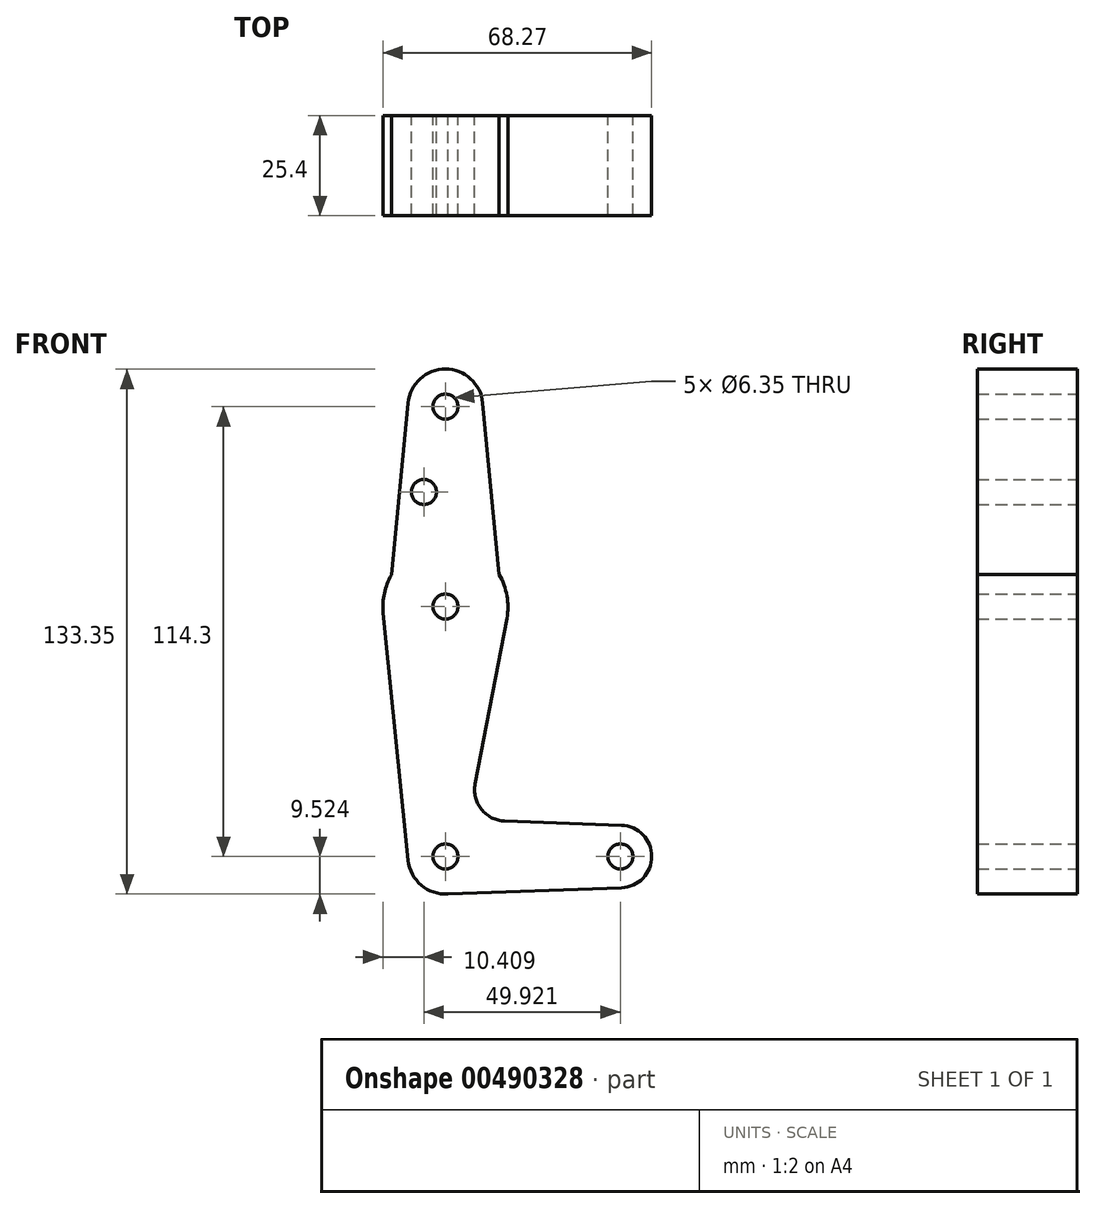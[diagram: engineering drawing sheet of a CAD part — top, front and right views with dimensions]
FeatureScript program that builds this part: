
annotation { "Feature Type Name" : "Feature", "Feature Type Description" : "" }
export const myFeature = defineFeature(function(context is Context, id is Id, definition is map)
    precondition{}
    {
        {
            var Q0;
            Q0=qCreatedBy(makeId("Front.planeOp"),FACE);
            var sketch = newSketch(context, id + "F0", { "sketchPlane" : qUnion([Q0])});
            skLineSegment(sketch, "E0", {"start": v(0, 62.8) * mm, "end": v(0, -51.5) * mm});
            skLineSegment(sketch, "E1", {"start": v(0, -51.5) * mm, "end": v(44.45, -51.5) * mm});
            skCircle(sketch, "E2", {"center": v(0, 62.8) * mm, "radius": 9.53 * mm});
            skCircle(sketch, "E3", {"center": v(0, 12) * mm, "radius": 15.88 * mm});
            skCircle(sketch, "E4", {"center": v(0, -51.5) * mm, "radius": 9.53 * mm});
            skCircle(sketch, "E5", {"center": v(44.45, -51.5) * mm, "radius": 7.94 * mm});
            skLineSegment(sketch, "E6", {"start": v(15.6, 9) * mm, "end": v(7.53, -33.08) * mm});
            skLineSegment(sketch, "E7", {"start": v(-9.48, 63.71) * mm, "end": v(-13.71, 20) * mm});
            skLineSegment(sketch, "E8", {"start": v(9.48, 63.7) * mm, "end": v(13.65, 20.1) * mm});
            skLineSegment(sketch, "E9", {"start": v(15.05, -42.52) * mm, "end": v(44.73, -43.57) * mm});
            skLineSegment(sketch, "E10", {"start": v(0, -61.03) * mm, "end": v(44.73, -59.44) * mm});
            skLineSegment(sketch, "E11", {"start": v(44.73, -59.44) * mm, "end": v(26.13, -60.1) * mm});
            skPoint(sketch, "E12.start.orphan", {"position": v(-10.4, 0) * mm});
            skArc(sketch, "E13.filletArc", {"start": v(7.53, -33.08) * mm, "mid": v(9.12, -39.53) * mm, "end": v(15.05, -42.52) * mm});
            skCircle(sketch, "E14", {"center": v(0, 62.8) * mm, "radius": 3.18 * mm});
            skCircle(sketch, "E15", {"center": v(0, 12) * mm, "radius": 3.17 * mm});
            skCircle(sketch, "E16", {"center": v(0, -51.5) * mm, "radius": 3.18 * mm});
            skCircle(sketch, "E17", {"center": v(44.45, -51.5) * mm, "radius": 3.18 * mm});
            skCircle(sketch, "E18", {"center": v(-5.47, 41.1) * mm, "radius": 3.18 * mm});
            skLineSegment(sketch, "E19", {"start": v(-15.8, 10.4) * mm, "end": v(-9.48, -52.46) * mm});
            skSolve(sketch);
        }
        {
            var Q0;
            Q0 = qSketchRegion(id + "F0", true);
            extrude(context, id + "F1", {"entities" : qUnion([Q0]), "depth" : 25.4 * mm});
        }
        {
            var Q0;
            {var subQ0=sQuery(id+"F0.wireOp",EDGE,"E4");var subQ1=sQuery(id+"F0.wireOp",EDGE,"E0");var subQ2=makeQuery(id+"F0.imprint","INTERSECT",VERTEX,{"derivedFrom":[subQ1,subQ0]});Q0=makeQuery(id+"F0.imprint","IMPRINT",FACE,{"disambiguationData":[TD([[makeQuery(id+"F0.imprint","IMPRINT",EDGE,{"disambiguationData":[TD([[subQ2,-1.0]])],"derivedFrom":subQ1}),1.0]])]});}
            extrude(context, id + "F2", {"entities" : qUnion([Q0]), "operationType" : NewBodyOperationType.ADD, "depth" : 25.4 * mm});
        }
    });
